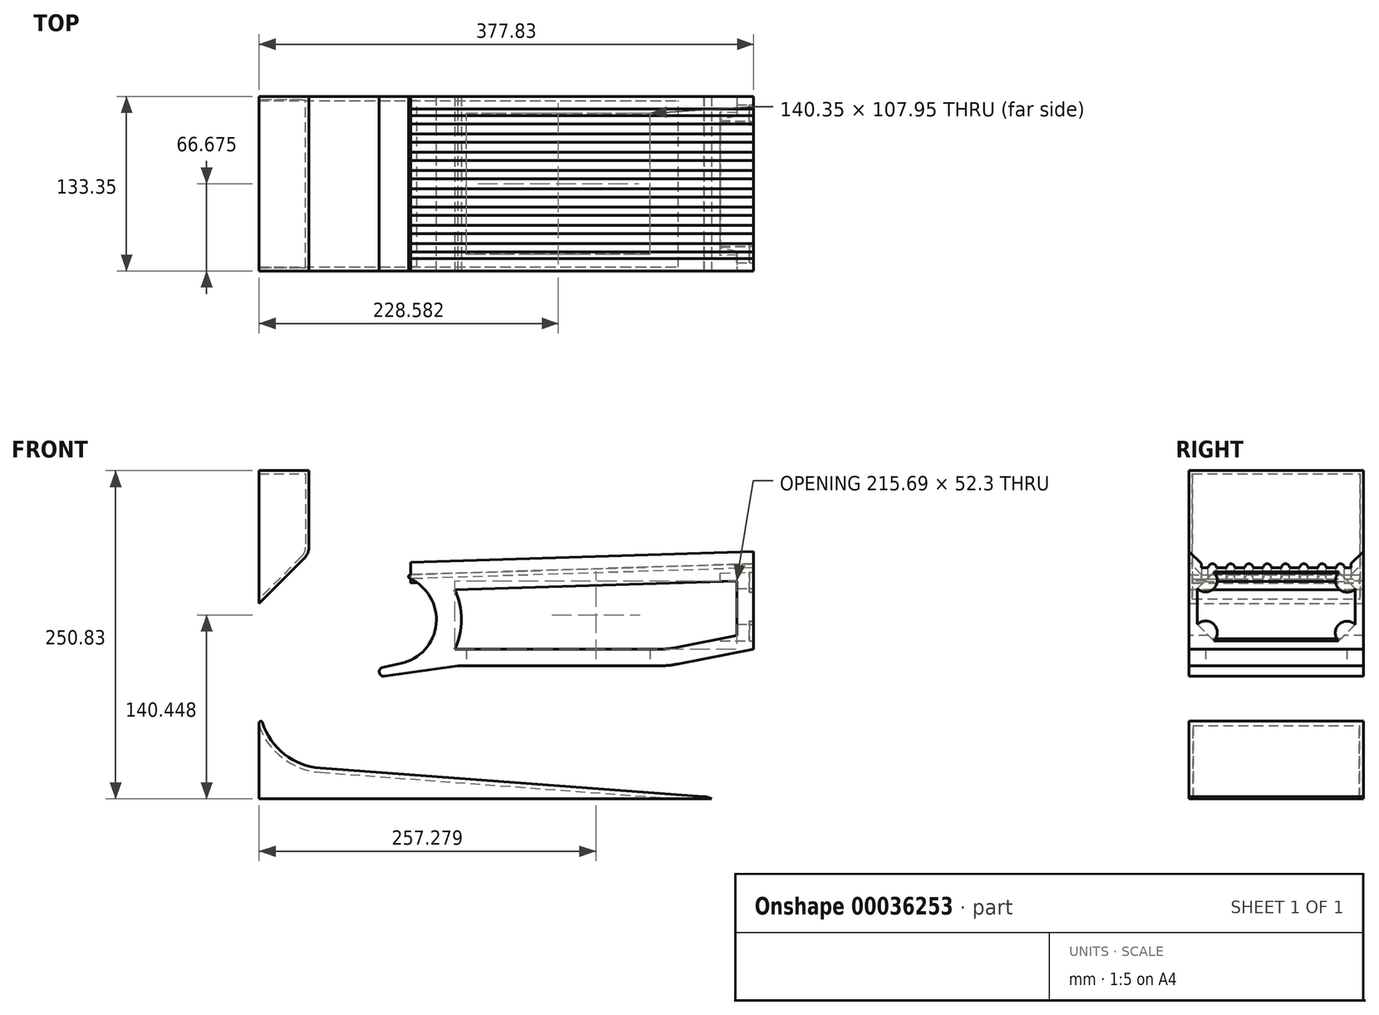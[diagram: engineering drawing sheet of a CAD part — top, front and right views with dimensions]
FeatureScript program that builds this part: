
annotation { "Feature Type Name" : "Feature", "Feature Type Description" : "" }
export const myFeature = defineFeature(function(context is Context, id is Id, definition is map)
    precondition{}
    {
        {
            var Q0;
            Q0=qCreatedBy(makeId("Front.planeOp"),FACE);
            var sketch = newSketch(context, id + "F0", { "sketchPlane" : qUnion([Q0])});
            skLineSegment(sketch, "E0.bottom", {"start": v(0, 0) * mm, "end": v(377.82, 0) * mm});
            skLineSegment(sketch, "E0.top", {"start": v(0, 250.83) * mm, "end": v(377.83, 250.83) * mm});
            skLineSegment(sketch, "E0.left", {"start": v(0, 74.15) * mm, "end": v(0, 250.82) * mm});
            skLineSegment(sketch, "E0.right", {"start": v(377.83, 0) * mm, "end": v(377.83, 250.83) * mm});
            skCircle(sketch, "E1", {"center": v(75.12, 58.13) * mm, "radius": 33.02 * mm});
            skArc(sketch, "E2", {"start": v(340.31, 1.68) * mm, "mid": v(359.23, 5.64) * mm, "end": v(373.15, 19.05) * mm});
            skLineSegment(sketch, "E3", {"start": v(377.83, 19.05) * mm, "end": v(373.15, 19.05) * mm});
            skLineSegment(sketch, "E4", {"start": v(47.03, 23.5) * mm, "end": v(340.31, 1.68) * mm});
            skPoint(sketch, "E5.visualSharp", {"position": v(0, 26.99) * mm});
            skArc(sketch, "E5.filletArc", {"start": v(2.48, 58.48) * mm, "mid": v(19.43, 34.2) * mm, "end": v(47.03, 23.5) * mm});
            skCircle(sketch, "E6.1.0.0", {"center": v(141.46, 52.73) * mm, "radius": 33.02 * mm});
            skCircle(sketch, "E6.2.0.0", {"center": v(207.8, 47.34) * mm, "radius": 33.02 * mm});
            skCircle(sketch, "E6.3.0.0", {"center": v(274.13, 41.94) * mm, "radius": 33.02 * mm});
            skCircle(sketch, "E6.4.0.0", {"center": v(340.47, 36.54) * mm, "radius": 33.02 * mm});
            skLineSegment(sketch, "E6.direction1", {"start": v(75.12, 58.13) * mm, "end": v(141.46, 52.73) * mm, "construction": true});
            skCircle(sketch, "E7", {"center": v(34.64, 111.21) * mm, "radius": 33.02 * mm});
            skLineSegment(sketch, "E8", {"start": v(377.83, 179.7) * mm, "end": v(115.72, 171.4) * mm});
            skArc(sketch, "E9.trimOffspring", {"start": v(108.42, 103.52) * mm, "mid": v(135.29, 133.5) * mm, "end": v(115.13, 168.36) * mm});
            skPoint(sketch, "E10.visualSharp", {"position": v(94.86, 170.74) * mm});
            skArc(sketch, "E10.filletArc", {"start": v(115.72, 171.4) * mm, "mid": v(114.21, 170.12) * mm, "end": v(115.13, 168.36) * mm});
            skCircle(sketch, "E11", {"center": v(96.26, 138.02) * mm, "radius": 33.02 * mm});
            skLineSegment(sketch, "E12", {"start": v(94.32, 100.47) * mm, "end": v(108.42, 103.52) * mm});
            skLineSegment(sketch, "E13", {"start": v(91.89, 96.7) * mm, "end": v(91.98, 96.26) * mm});
            skLineSegment(sketch, "E14", {"start": v(95.52, 93.78) * mm, "end": v(152.06, 101.6) * mm});
            skPoint(sketch, "E15.visualSharp", {"position": v(91.22, 99.8) * mm});
            skArc(sketch, "E15.filletArc", {"start": v(94.32, 100.47) * mm, "mid": v(92.32, 99.09) * mm, "end": v(91.89, 96.7) * mm});
            skPoint(sketch, "E16.visualSharp", {"position": v(92.6, 93.38) * mm});
            skArc(sketch, "E16.filletArc", {"start": v(91.98, 96.26) * mm, "mid": v(93.26, 94.32) * mm, "end": v(95.52, 93.78) * mm});
            skCircle(sketch, "E17.1.0.0", {"center": v(139.77, 207.48) * mm, "radius": 33.02 * mm});
            skCircle(sketch, "E17.2.0.0", {"center": v(206.9, 209.08) * mm, "radius": 33.02 * mm});
            skCircle(sketch, "E17.3.0.0", {"center": v(274.03, 210.68) * mm, "radius": 33.02 * mm});
            skCircle(sketch, "E17.4.0.0", {"center": v(341.17, 212.28) * mm, "radius": 33.02 * mm});
            skLineSegment(sketch, "E17.direction1", {"start": v(72.64, 205.88) * mm, "end": v(139.77, 207.48) * mm, "construction": true});
            skCircle(sketch, "E18.1.0.0", {"center": v(72.02, 201.09) * mm, "radius": 33.02 * mm});
            skLineSegment(sketch, "E19", {"start": v(38.1, 250.83) * mm, "end": v(38.1, 192.59) * mm});
            skLineSegment(sketch, "E20", {"start": v(34.38, 183.6) * mm, "end": v(0, 149.22) * mm});
            skPoint(sketch, "E21.visualSharp", {"position": v(38.1, 187.32) * mm});
            skArc(sketch, "E21.filletArc", {"start": v(34.38, 183.6) * mm, "mid": v(37.13, 187.73) * mm, "end": v(38.1, 192.59) * mm});
            skLineSegment(sketch, "E22", {"start": v(0, 0) * mm, "end": v(0, 58.09) * mm});
            skCircle(sketch, "E23", {"center": v(374.8, 54.39) * mm, "radius": 33.02 * mm});
            skLineSegment(sketch, "E24", {"start": v(305.1, 101.6) * mm, "end": v(152.06, 101.6) * mm});
            skPoint(sketch, "E25.orphan", {"position": v(312.44, 101.6) * mm});
            skLineSegment(sketch, "E26", {"start": v(319.64, 103) * mm, "end": v(377.83, 114.3) * mm});
            skPoint(sketch, "E27.orphan", {"position": v(377.83, 101.6) * mm});
            skArc(sketch, "E28.filletArc", {"start": v(305.1, 101.6) * mm, "mid": v(312.4, 101.95) * mm, "end": v(319.64, 103) * mm});
            skPoint(sketch, "E29.visualSharp", {"position": v(0, 74.15) * mm});
            skArc(sketch, "E29.filletArc", {"start": v(2.48, 58.48) * mm, "mid": v(1.07, 59.34) * mm, "end": v(0, 58.09) * mm});
            skSolve(sketch);
        }
        {
            var Q0;
            {var subQ2=sQuery(id+"F0.wireOp",EDGE,"E0.bottom");Q0=makeQuery(id+"F0.imprint","IMPRINT",FACE,{"disambiguationData":[TD([[makeQuery(id+"F0.imprint","IMPRINT",EDGE,{"derivedFrom":subQ2}),1.0]])]});}
            var Q1;
            {var subQ1=sQuery(id+"F0.wireOp",EDGE,"E8");Q1=makeQuery(id+"F0.imprint","IMPRINT",FACE,{"disambiguationData":[TD([[makeQuery(id+"F0.imprint","IMPRINT",EDGE,{"derivedFrom":subQ1}),1.0]])]});}
            var Q2;
            {var subQ1=sQuery(id+"F0.wireOp",EDGE,"E19");Q2=makeQuery(id+"F0.imprint","IMPRINT",FACE,{"disambiguationData":[TD([[makeQuery(id+"F0.imprint","IMPRINT",EDGE,{"derivedFrom":subQ1}),-1.0]])]});}
            extrude(context, id + "F1", {"entities" : qUnion([Q0, Q1, Q2]), "depth" : 133.35 * mm});
        }
        {
            var Q0;
            {var subQ0=sQuery(id+"F0.wireOp",EDGE,"E0.right");Q0=makeQuery(id+"F1.opExtrude","SWEPT_FACE",FACE,{"disambiguationData":[OSD([subQ0]),TDD([makeQuery(id+"F0.imprint","IMPRINT",EDGE,{"disambiguationData":[TD([[makeQuery(id+"F0.imprint","INTERSECT",VERTEX,{"derivedFrom":[subQ0,sQuery(id+"F0.wireOp",EDGE,"E8")]}),1.0]])],"derivedFrom":subQ0})])]});}
            var sketch = newSketch(context, id + "F2", { "sketchPlane" : qUnion([Q0])});
            skLineSegment(sketch, "E30.bottom", {"start": v(0, 179.7) * mm, "end": v(-98.4, 179.7) * mm});
            skLineSegment(sketch, "E30.top", {"start": v(0, 188.78) * mm, "end": v(-98.4, 188.78) * mm});
            skLineSegment(sketch, "E30.left", {"start": v(0, 179.7) * mm, "end": v(0, 188.78) * mm});
            skLineSegment(sketch, "E30.right", {"start": v(-98.4, 179.7) * mm, "end": v(-98.4, 188.78) * mm});
            skSolve(sketch);
        }
        {
            var Q0;
            Q0=makeQuery(id+"F1.opExtrude","CAP_FACE",FACE,{"disambiguationData":[OSD([sQuery(id+"F0.wireOp",EDGE,"E0.right"),sQuery(id+"F0.wireOp",EDGE,"E8"),sQuery(id+"F0.wireOp",EDGE,"E9.trimOffspring"),sQuery(id+"F0.wireOp",EDGE,"E10.filletArc"),sQuery(id+"F0.wireOp",EDGE,"E12"),sQuery(id+"F0.wireOp",EDGE,"E13"),sQuery(id+"F0.wireOp",EDGE,"E14"),sQuery(id+"F0.wireOp",EDGE,"E15.filletArc"),sQuery(id+"F0.wireOp",EDGE,"E16.filletArc"),sQuery(id+"F0.wireOp",EDGE,"E24"),sQuery(id+"F0.wireOp",EDGE,"E26"),sQuery(id+"F0.wireOp",EDGE,"E28.filletArc")])],"isStart":false});
            var sketch = newSketch(context, id + "F3", { "sketchPlane" : qUnion([Q0])});
            skLineSegment(sketch, "E31.0", {"start": v(365.13, 166.6) * mm, "end": v(149.44, 159.76) * mm});
            skLineSegment(sketch, "E32.0", {"start": v(305.1, 114.3) * mm, "end": v(149.43, 114.3) * mm});
            skArc(sketch, "E32.1", {"start": v(305.1, 114.3) * mm, "mid": v(311.19, 114.6) * mm, "end": v(317.21, 115.46) * mm});
            skLineSegment(sketch, "E32.2", {"start": v(317.21, 115.46) * mm, "end": v(365.13, 124.77) * mm});
            skLineSegment(sketch, "E32.3", {"start": v(365.13, 124.77) * mm, "end": v(365.13, 166.6) * mm});
            skArc(sketch, "E33.0", {"start": v(149.43, 114.3) * mm, "mid": v(154.52, 137.03) * mm, "end": v(149.44, 159.76) * mm});
            skSolve(sketch);
        }
        {
            var Q0;
            {var subQ6=sQuery(id+"F2.wireOp",EDGE,"E30.bottom");Q0=makeQuery(id+"F2.imprint","IMPRINT",FACE,{"disambiguationData":[TD([[makeQuery(id+"F2.imprint","IMPRINT",EDGE,{"derivedFrom":subQ6}),-1.0]])]});}
            var sketch = newSketch(context, id + "F4", { "sketchPlane" : qUnion([Q0])});
            skLineSegment(sketch, "E34.bottom", {"start": v(-114.3, 173.36) * mm, "end": v(-19.05, 173.36) * mm});
            skLineSegment(sketch, "E34.top", {"start": v(-114.3, 120.65) * mm, "end": v(-19.05, 120.65) * mm});
            skLineSegment(sketch, "E34.left", {"start": v(-127, 160.66) * mm, "end": v(-127, 133.35) * mm});
            skLineSegment(sketch, "E34.right", {"start": v(-6.35, 160.66) * mm, "end": v(-6.35, 133.35) * mm});
            skLineSegment(sketch, "E35", {"start": v(-127, 160.66) * mm, "end": v(-114.3, 173.36) * mm});
            skPoint(sketch, "E36.orphan", {"position": v(-127, 173.36) * mm});
            skLineSegment(sketch, "E37.MirrorCS", {"start": v(-6.35, 160.66) * mm, "end": v(-19.05, 173.36) * mm});
            skLineSegment(sketch, "E38.MirrorCS", {"start": v(-6.35, 133.35) * mm, "end": v(-19.05, 120.65) * mm});
            skPoint(sketch, "E39.start.orphan", {"position": v(-6.35, 147) * mm});
            skPoint(sketch, "E40.start.orphan", {"position": v(-66.68, 120.65) * mm});
            skPoint(sketch, "E41.orphan", {"position": v(-127, 120.65) * mm});
            skPoint(sketch, "E42.orphan", {"position": v(-6.35, 120.65) * mm});
            skPoint(sketch, "E43.orphan", {"position": v(-6.35, 173.36) * mm});
            skLineSegment(sketch, "E44.MirrorCS", {"start": v(-127, 133.35) * mm, "end": v(-114.3, 120.65) * mm});
            skPoint(sketch, "E45.end.orphan", {"position": v(-127, 147) * mm});
            skSolve(sketch);
        }
        {
            var Q0;
            Q0=makeQuery(id+"F1.opExtrude","CAP_FACE",FACE,{"disambiguationData":[OSD([sQuery(id+"F0.wireOp",EDGE,"E0.bottom"),sQuery(id+"F0.wireOp",EDGE,"E0.right"),sQuery(id+"F0.wireOp",EDGE,"E2"),sQuery(id+"F0.wireOp",EDGE,"E3"),sQuery(id+"F0.wireOp",EDGE,"E4"),sQuery(id+"F0.wireOp",EDGE,"E5.filletArc"),sQuery(id+"F0.wireOp",EDGE,"E22")])],"isStart":false});
            var sketch = newSketch(context, id + "F5", { "sketchPlane" : qUnion([Q0])});
            skLineSegment(sketch, "E46.bottom", {"start": v(377.83, 0) * mm, "end": v(345.84, 0) * mm});
            skLineSegment(sketch, "E46.top", {"start": v(377.83, 22.34) * mm, "end": v(345.84, 22.34) * mm});
            skLineSegment(sketch, "E46.left", {"start": v(377.83, 0) * mm, "end": v(377.83, 22.34) * mm});
            skLineSegment(sketch, "E46.right", {"start": v(345.84, 4.83) * mm, "end": v(345.84, 22.34) * mm});
            skLineSegment(sketch, "E47", {"start": v(345.84, 0) * mm, "end": v(345.64, 0.1) * mm});
            skLineSegment(sketch, "E48", {"start": v(340.31, 1.68) * mm, "end": v(339.94, 1.7) * mm});
            skPoint(sketch, "E49.visualSharp", {"position": v(342.98, 1.59) * mm});
            skArc(sketch, "E49.filletArc", {"start": v(345.64, 0.1) * mm, "mid": v(342.88, 1.24) * mm, "end": v(339.94, 1.7) * mm});
            skLineSegment(sketch, "E50", {"start": v(339.94, 1.7) * mm, "end": v(345.84, 4.83) * mm});
            skSolve(sketch);
        }
        {
            var Q0;
            Q0=qSketchRegion(id+"F5",true);
            extrude(context, id + "F6", {"entities" : qUnion([Q0]), "operationType" : NewBodyOperationType.REMOVE, "endBound" : BoundingType.THROUGH_ALL, "oppositeDirection" : true, "depth" : 25.4 * mm});
        }
        {
            var Q0;
            Q0=makeQuery(id+"F1.opExtrude","SWEPT_FACE",FACE,{"disambiguationData":[OSD([sQuery(id+"F0.wireOp",EDGE,"E0.left")])]});
            shell(context, id + "F7", {"entities" : qUnion([Q0]), "thickness" : 2.54 * mm});
        }
        {
            var Q0;
            {var subQ6=sQuery(id+"F2.wireOp",EDGE,"E30.bottom");Q0=makeQuery(id+"F2.imprint","IMPRINT",FACE,{"disambiguationData":[TD([[makeQuery(id+"F2.imprint","IMPRINT",EDGE,{"derivedFrom":subQ6}),-1.0]])]});}
            var sketch = newSketch(context, id + "F8", { "sketchPlane" : qUnion([Q0])});
            skLineSegment(sketch, "E51", {"start": v(-123.83, 176.53) * mm, "end": v(-118.74, 176.53) * mm});
            skArc(sketch, "E52", {"start": v(-112.4, 176.53) * mm, "mid": v(-115.57, 179.7) * mm, "end": v(-118.75, 176.53) * mm});
            skArc(sketch, "E53.1.0.0", {"start": v(-98.43, 176.53) * mm, "mid": v(-101.6, 179.7) * mm, "end": v(-104.78, 176.53) * mm});
            skArc(sketch, "E53.2.0.0", {"start": v(-84.46, 176.53) * mm, "mid": v(-87.63, 179.7) * mm, "end": v(-90.8, 176.53) * mm});
            skArc(sketch, "E53.3.0.0", {"start": v(-70.49, 176.53) * mm, "mid": v(-73.66, 179.7) * mm, "end": v(-76.84, 176.53) * mm});
            skArc(sketch, "E53.4.0.0", {"start": v(-56.52, 176.53) * mm, "mid": v(-59.7, 179.7) * mm, "end": v(-62.87, 176.53) * mm});
            skArc(sketch, "E53.5.0.0", {"start": v(-42.55, 176.53) * mm, "mid": v(-45.72, 179.7) * mm, "end": v(-48.9, 176.53) * mm});
            skArc(sketch, "E53.6.0.0", {"start": v(-28.58, 176.53) * mm, "mid": v(-31.75, 179.7) * mm, "end": v(-34.93, 176.53) * mm});
            skArc(sketch, "E53.7.0.0", {"start": v(-14.6, 176.53) * mm, "mid": v(-17.78, 179.7) * mm, "end": v(-20.96, 176.53) * mm});
            skLineSegment(sketch, "E53.direction1", {"start": v(-112.4, 176.53) * mm, "end": v(-101.6, 176.53) * mm, "construction": true});
            skLineSegment(sketch, "E54.trimOffspring", {"start": v(-112.4, 176.53) * mm, "end": v(-104.78, 176.53) * mm});
            skLineSegment(sketch, "E55.trimOffspring", {"start": v(-70.49, 176.53) * mm, "end": v(-62.87, 176.53) * mm});
            skLineSegment(sketch, "E56.trimOffspring", {"start": v(-28.58, 176.53) * mm, "end": v(-20.96, 176.53) * mm});
            skLineSegment(sketch, "E57.trimOffspring", {"start": v(-14.6, 176.53) * mm, "end": v(-9.53, 176.53) * mm});
            skLineSegment(sketch, "E58", {"start": v(-42.55, 176.53) * mm, "end": v(-34.93, 176.53) * mm});
            skLineSegment(sketch, "E59", {"start": v(-56.52, 176.53) * mm, "end": v(-48.9, 176.53) * mm});
            skLineSegment(sketch, "E60", {"start": v(-84.46, 176.53) * mm, "end": v(-76.84, 176.53) * mm});
            skLineSegment(sketch, "E61", {"start": v(-98.43, 176.53) * mm, "end": v(-90.8, 176.53) * mm});
            skLineSegment(sketch, "E62", {"start": v(-123.83, 176.53) * mm, "end": v(-123.83, 179.7) * mm});
            skLineSegment(sketch, "E63", {"start": v(-115.57, 179.7) * mm, "end": v(-123.83, 179.7) * mm});
            skLineSegment(sketch, "E64", {"start": v(-115.57, 179.7) * mm, "end": v(-9.52, 179.7) * mm});
            skLineSegment(sketch, "E65", {"start": v(-9.53, 176.53) * mm, "end": v(-9.53, 179.7) * mm});
            skPoint(sketch, "E66.orphan", {"position": v(0, 176.53) * mm});
            skPoint(sketch, "E67.orphan", {"position": v(0, 179.7) * mm});
            skPoint(sketch, "E68.start.orphan", {"position": v(-133.35, 176.53) * mm});
            skSolve(sketch);
        }
        {
            var Q0;
            Q0=qSketchRegion(id+"F8",true);
            var Q1;
            Q1=makeQuery(id+"F1.opExtrude","CAP_EDGE",EDGE,{"disambiguationData":[OSD([sQuery(id+"F0.wireOp",EDGE,"E8")])],"isStart":false});
            sweep(context, id + "F9", {"operationType" : NewBodyOperationType.REMOVE, "profiles" : qUnion([Q0]), "path" : qUnion([Q1])});
        }
        {
            var Q0;
            {var subQ6=sQuery(id+"F2.wireOp",EDGE,"E30.bottom");Q0=makeQuery(id+"F2.imprint","IMPRINT",FACE,{"disambiguationData":[TD([[makeQuery(id+"F2.imprint","IMPRINT",EDGE,{"derivedFrom":subQ6}),-1.0]])]});}
            var sketch = newSketch(context, id + "F10", { "sketchPlane" : qUnion([Q0])});
            skLineSegment(sketch, "E69", {"start": v(-133.35, 189.1) * mm, "end": v(-133.35, 179.58) * mm});
            skLineSegment(sketch, "E70", {"start": v(-133.35, 179.58) * mm, "end": v(-123.83, 179.58) * mm});
            skLineSegment(sketch, "E71", {"start": v(-123.83, 179.58) * mm, "end": v(-123.83, 179.7) * mm});
            skLineSegment(sketch, "E72", {"start": v(-123.83, 179.7) * mm, "end": v(-133.35, 189.1) * mm});
            skLineSegment(sketch, "E73.MirrorCS", {"start": v(-9.52, 179.7) * mm, "end": v(0, 189.1) * mm});
            skLineSegment(sketch, "E74.MirrorCS", {"start": v(-9.52, 179.58) * mm, "end": v(-9.52, 179.7) * mm});
            skLineSegment(sketch, "E75.MirrorCS", {"start": v(0, 179.58) * mm, "end": v(-9.53, 179.58) * mm});
            skLineSegment(sketch, "E76.MirrorCS", {"start": v(0, 189.1) * mm, "end": v(0, 179.58) * mm});
            skSolve(sketch);
        }
        {
            var Q0;
            Q0=qSketchRegion(id+"F10",true);
            var Q1;
            Q1=makeQuery(id+"F1.opExtrude","CAP_EDGE",EDGE,{"disambiguationData":[OSD([sQuery(id+"F0.wireOp",EDGE,"E8")])],"isStart":false});
            sweep(context, id + "F11", {"operationType" : NewBodyOperationType.ADD, "profiles" : qUnion([Q0]), "path" : qUnion([Q1])});
        }
        {
            var Q0;
            Q0=qSketchRegion(id+"F3",true);
            extrude(context, id + "F12", {"entities" : qUnion([Q0]), "operationType" : NewBodyOperationType.REMOVE, "endBound" : BoundingType.THROUGH_ALL, "oppositeDirection" : true, "depth" : 25.4 * mm});
        }
        {
            var Q0;
            Q0=qSketchRegion(id+"F4",true);
            extrude(context, id + "F13", {"entities" : qUnion([Q0]), "operationType" : NewBodyOperationType.REMOVE, "oppositeDirection" : true, "depth" : 25.4 * mm});
        }
        {
            var Q0;
            Q0=qCreatedBy(makeId("Right.planeOp"),FACE);
            cPlane(context, id + "F14", {"entities" : qUnion([Q0]), "cplaneType" : CPlaneType.OFFSET, "offset" : 339.72 * mm, "width" : 152.4 * mm, "height" : 152.4 * mm});
        }
        {
            var Q0;
            Q0=makeQuery(id+"F1.opExtrude","SWEPT_FACE",FACE,{"disambiguationData":[OSD([sQuery(id+"F0.wireOp",EDGE,"E0.bottom")])]});
            var Q1;
            Q1=makeQuery(id+"F1.opExtrude","SWEPT_FACE",FACE,{"disambiguationData":[OSD([sQuery(id+"F0.wireOp",EDGE,"E22")])]});
            shell(context, id + "F15", {"entities" : qUnion([Q0, Q1]), "thickness" : 3.17 * mm});
        }
        {
            var Q0;
            {var subQ0=sQuery(id+"F0.wireOp",EDGE,"E8");Q0=makeQuery(id+"F11.boolean.opBoolean","MERGE",FACE,{"derivedFrom":[makeQuery(id+"F1.opExtrude","CAP_FACE",FACE,{"disambiguationData":[OSD([sQuery(id+"F0.wireOp",EDGE,"E0.right"),subQ0,sQuery(id+"F0.wireOp",EDGE,"E9.trimOffspring"),sQuery(id+"F0.wireOp",EDGE,"E10.filletArc"),sQuery(id+"F0.wireOp",EDGE,"E12"),sQuery(id+"F0.wireOp",EDGE,"E13"),sQuery(id+"F0.wireOp",EDGE,"E14"),sQuery(id+"F0.wireOp",EDGE,"E15.filletArc"),sQuery(id+"F0.wireOp",EDGE,"E16.filletArc"),sQuery(id+"F0.wireOp",EDGE,"E24"),sQuery(id+"F0.wireOp",EDGE,"E26"),sQuery(id+"F0.wireOp",EDGE,"E28.filletArc")])],"isStart":true}),makeQuery(id+"F11.opSweep","SWEPT_FACE",FACE,{"disambiguationData":[OSD([subQ0,sQuery(id+"F10.wireOp",EDGE,"E76.MirrorCS")])]})]});}
            cPlane(context, id + "F16", {"entities" : qUnion([Q0]), "cplaneType" : CPlaneType.OFFSET, "offset" : 66.67 * mm, "oppositeDirection" : true, "width" : 152.4 * mm, "height" : 152.4 * mm});
        }
        {
            var Q0;
            Q0=makeQuery(id+"F9.boolean.opBoolean","COPY",FACE,{"derivedFrom":makeQuery(id+"F9.opSweep","SWEPT_FACE",FACE,{"disambiguationData":[OSD([sQuery(id+"F0.wireOp",EDGE,"E8"),sQuery(id+"F8.wireOp",EDGE,"E60")])]})});
            var sketch = newSketch(context, id + "F17", { "sketchPlane" : qUnion([Q0])});
            skLineSegment(sketch, "E77.bottom", {"start": v(121, -130.18) * mm, "end": v(383.33, -130.17) * mm});
            skLineSegment(sketch, "E77.top", {"start": v(121, -3.18) * mm, "end": v(383.33, -3.17) * mm});
            skLineSegment(sketch, "E77.left", {"start": v(121, -130.18) * mm, "end": v(121, -3.18) * mm});
            skLineSegment(sketch, "E77.right", {"start": v(383.33, -130.17) * mm, "end": v(383.33, -3.17) * mm});
            skSolve(sketch);
        }
        {
            var Q0;
            Q0=qSketchRegion(id+"F17",true);
            extrude(context, id + "F18", {"entities" : qUnion([Q0]), "operationType" : NewBodyOperationType.ADD, "oppositeDirection" : true, "depth" : 3.17 * mm});
        }
        {
            var Q0;
            {var subQ16=sQuery(id+"F8.wireOp",EDGE,"E51");Q0=makeQuery(id+"F8.imprint","IMPRINT",FACE,{"disambiguationData":[TD([[makeQuery(id+"F8.imprint","IMPRINT",EDGE,{"derivedFrom":subQ16}),-1.0]])]});}
            var sketch = newSketch(context, id + "F19", { "sketchPlane" : qUnion([Q0])});
            skLineSegment(sketch, "E78.bottom", {"start": v(-138.63, 187.5) * mm, "end": v(18.2, 187.5) * mm});
            skLineSegment(sketch, "E78.top", {"start": v(-138.63, 162.02) * mm, "end": v(18.2, 162.02) * mm});
            skLineSegment(sketch, "E78.left", {"start": v(-138.63, 187.5) * mm, "end": v(-138.63, 162.02) * mm});
            skLineSegment(sketch, "E78.right", {"start": v(18.2, 187.5) * mm, "end": v(18.2, 162.02) * mm});
            skSolve(sketch);
        }
        {
            var Q0;
            Q0=qSketchRegion(id+"F19",true);
            extrude(context, id + "F20", {"entities" : qUnion([Q0]), "operationType" : NewBodyOperationType.REMOVE, "depth" : 25.4 * mm});
        }
        {
            var Q0;
            {var subQ16=sQuery(id+"F8.wireOp",EDGE,"E51");Q0=makeQuery(id+"F8.imprint","IMPRINT",FACE,{"disambiguationData":[TD([[makeQuery(id+"F8.imprint","IMPRINT",EDGE,{"derivedFrom":subQ16}),-1.0]])]});}
            var sketch = newSketch(context, id + "F21", { "sketchPlane" : qUnion([Q0])});
            skCircle(sketch, "E79", {"center": v(-120.76, 166.98) * mm, "radius": 8.9 * mm});
            skCircle(sketch, "E80", {"center": v(-12.75, 126.92) * mm, "radius": 8.9 * mm});
            skCircle(sketch, "E81", {"center": v(-12.67, 166.9) * mm, "radius": 8.9 * mm});
            skCircle(sketch, "E82", {"center": v(-120.72, 127.06) * mm, "radius": 8.9 * mm});
            skSolve(sketch);
        }
        {
            var Q0;
            Q0=qSketchRegion(id+"F21",true);
            extrude(context, id + "F22", {"entities" : qUnion([Q0]), "operationType" : NewBodyOperationType.ADD, "oppositeDirection" : true, "depth" : 3.17 * mm});
        }
        {
            var Q0;
            Q0=makeQuery(id+"F1.opExtrude","SWEPT_FACE",FACE,{"disambiguationData":[OSD([sQuery(id+"F0.wireOp",EDGE,"E24")])]});
            var sketch = newSketch(context, id + "F23", { "sketchPlane" : qUnion([Q0])});
            skLineSegment(sketch, "E83.0", {"start": v(298.76, 120.65) * mm, "end": v(158.4, 120.65) * mm});
            skLineSegment(sketch, "E84.0", {"start": v(158.4, 12.7) * mm, "end": v(298.76, 12.7) * mm});
            skLineSegment(sketch, "E85.0", {"start": v(158.4, 120.65) * mm, "end": v(158.4, 12.7) * mm});
            skLineSegment(sketch, "E86.0", {"start": v(298.76, 120.65) * mm, "end": v(298.76, 12.7) * mm});
            skSolve(sketch);
        }
        {
            var Q0;
            Q0=qSketchRegion(id+"F23",true);
            extrude(context, id + "F24", {"entities" : qUnion([Q0]), "operationType" : NewBodyOperationType.REMOVE, "oppositeDirection" : true, "depth" : 25.4 * mm});
        }
        {
            var Q0;
            Q0=qCreatedBy(id+"F16.planeOp",FACE);
            var sketch = newSketch(context, id + "F25", { "sketchPlane" : qUnion([Q0])});
            skLineSegment(sketch, "E87.bottom", {"start": v(-402.1, 228.81) * mm, "end": v(-71.6, 228.81) * mm});
            skLineSegment(sketch, "E87.top", {"start": v(-402.1, 62.7) * mm, "end": v(-71.6, 62.7) * mm});
            skLineSegment(sketch, "E87.left", {"start": v(-402.1, 228.81) * mm, "end": v(-402.1, 62.7) * mm});
            skLineSegment(sketch, "E87.right", {"start": v(-71.6, 228.81) * mm, "end": v(-71.6, 62.7) * mm});
            skSolve(sketch);
        }
        {
            var Q0;
            Q0=makeQuery(id+"F1.opExtrude","SWEPT_BODY",BODY,{"disambiguationData":[OSD([sQuery(id+"F0.wireOp",EDGE,"E0.bottom"),sQuery(id+"F0.wireOp",EDGE,"E0.right"),sQuery(id+"F0.wireOp",EDGE,"E2"),sQuery(id+"F0.wireOp",EDGE,"E3"),sQuery(id+"F0.wireOp",EDGE,"E4"),sQuery(id+"F0.wireOp",EDGE,"E5.filletArc"),sQuery(id+"F0.wireOp",EDGE,"E22"),sQuery(id+"F0.wireOp",EDGE,"E29.filletArc")])]});
            transform(context, id + "F26", {"entities" : qUnion([Q0]), "transformType" : TransformType.TRANSLATION_3D, "dx" : 0 * mm, "dy" : 0 * mm, "dz" : 0 * mm, "makeCopy" : true});
        }
        {
            var Q0;
            Q0=qSketchRegion(id+"F3",true);
            extrude(context, id + "F27", {"entities" : qUnion([Q0]), "operationType" : NewBodyOperationType.REMOVE, "endBound" : BoundingType.THROUGH_ALL, "oppositeDirection" : true, "depth" : 25.4 * mm});
        }
    });
